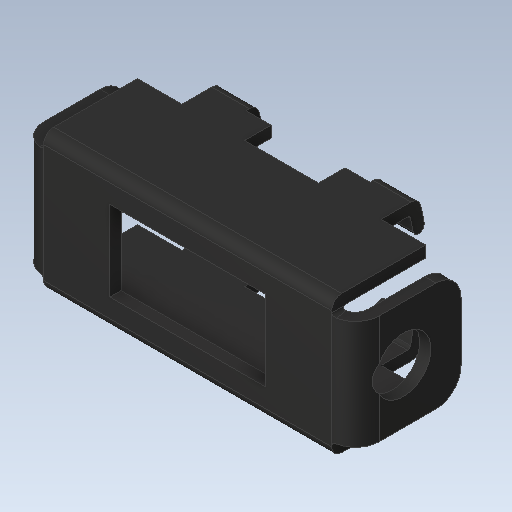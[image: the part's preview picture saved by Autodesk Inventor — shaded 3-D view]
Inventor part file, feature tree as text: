
AUTODESK INVENTOR PART (.ipt)
format: ipt  version: 2020.1 (Build 241239000, 239)  size: 246,784 bytes
history: native  units: mm
features: other x3, sketch x2
ambient origin geometry x8: Origin, YZ Plane, XZ Plane, XY Plane, X Axis, Y Axis, Z Axis, Center Point
bodies: Solid1 (feature_tree)
feature tree (5):
  other  "Bend Part1"
  other  "Bend Part2"
  sketch  "Sketch1"  dims[d0=0.5mm d1=90.0deg]
  sketch  "Sketch3"  dims[d2=0.5mm d3=90.0deg]
  other  "PartBody"
